# Revit family: VLGFS150xxOSxx
name_source: partatom
category: Leuchten
units: mm (PartAtom-declared; Revit-internal decimal feet)

## family parameters
Basisbauteil = Fläche
Beim Laden mit Abzugskörper schneiden = Nein
Bemaßung runder Anschluss = Durchmesser verwenden
Gemeinsam genutzt = Nein
Lichtquelle = Ja
OmniClass-Nummer = 23.80.70.11
OmniClass-Titel = Luminaries for Internal Lighting
Raumberechnungspunkt = Nein
Teiletyp = Normal

## types (16) — shared parameters
Baugruppenkennzeichen = D5020200
Datei für fotometrisches Netz = VLGFS1xxxOS.IES
Emissionsform beim Rendern sichtbar = Nein
Farbfilter = 16777215
Farbtemperaturverschiebung bei Dämpfen der Lampe = <Keine Auswahl>
Hersteller = RIDI Leuchten GmbH
Lampe = LED
Neigungswinkel = 90.00°
URL = www.ridi.de
Von Breite des Rechtecks ausssenden = 1477 mm  [stored 4.8458 ft]
Von Länge des Rechtecks aussenden = 94 mm  [stored 0.308399 ft]
brand = RIDI
conformity mark = CE
electrical safety class = 1
height = 74 mm  [stored 0.242782 ft]
ingress protection (IP) code = IP54
length = 1500 mm  [stored 4.92126 ft]
nominal frequency = 50-60Hz
nominal voltage = 230
voltage type (AC, DC, UC) = AC
width = 97 mm  [stored 0.318241 ft]
zero-valued in all types: Vorgabe-Ansicht

## per-type parameters (varying)
| type | Modell | Scheinlast | rated input power | weight |
| VLGFS1501-5NDWS830OS0700-RF | 1551281 | 60 VA | 60 | 2,88 kg |
| VLGFS1501-5NDWS840OS0700-RF | 1551282 | 60 VA | 60 | 2,88 kg |
| VLGFS1501-5NDWS850OS0750-RF | 1551283 | 60 VA | 60 | 2,88 kg |
| VLGFS1501-5NDWS865OS0700-RF | 1551284 | 60 VA | 60 | 2,88 kg |
| VLGFS1501-7DAWS830OS0700 | 1561185 | 61 VA | 61 | 2,88 kg |
| VLGFS1501-7DAWS840OS0750 | 1561182 | 61 VA | 61 | 2,88 kg |
| VLGFS1501-7DAWS850OS0800 | 1561188 | 61 VA | 61 | 2,88 kg |
| VLGFS1501-7DAWS865OS0750 | 1561191 | 61 VA | 61 | 2,88 kg |
| VLGFS1502-5NDWS830OS1400 | 1551240 | 122 VA | 122 | 3,32 kg |
| VLGFS1502-5NDWS840OS1500 | 1551237 | 122 VA | 122 | 3,32 kg |
| VLGFS1502-5NDWS850OS1600 | 1551243 | 122 VA | 122 | 3,32 kg |
| VLGFS1502-5NDWS865OS1500 | 1551246 | 122 VA | 122 | 3,32 kg |
| VLGFS1502-7DAWS830OS1400 | 1561240 | 122 VA | 122 | 3,32 kg |
| VLGFS1502-7DAWS840OS1500 | 1561237 | 122 VA | 122 | 3,32 kg |
| VLGFS1502-7DAWS850OS1600 | 1561243 | 122 VA | 122 | 3,32 kg |
| VLGFS1502-7DAWS865OS1500 | 1561246 | 122 VA | 122 | 3,32 kg |

note: column(s) folded — value = type name in every type: product name

note: [stored X ft] marks values corroborated as IEEE doubles in the binary element streams (Revit-internal decimal feet)
